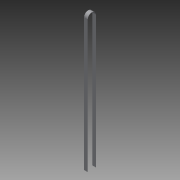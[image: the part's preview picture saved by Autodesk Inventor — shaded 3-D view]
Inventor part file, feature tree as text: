
AUTODESK INVENTOR PART (.ipt)
format: ipt  version: 2013 (Build 170138000, 138)  size: 89,088 bytes
history: native  units: in
note: dims shown in document units (in); Inventor stores cm internally (conversion verified against a paired STEP export)
features: extrude x1, sketch x1
ambient origin geometry x8: Origin, YZ Plane, XZ Plane, XY Plane, X Axis, Y Axis, Z Axis, Center Point
feature tree (2):
  extrude  "Extrusion2"  Depth=36.0in
  sketch  "Sketch1"  dims[d6=1.1in d7=36.0in d12=0.01in d13=1.0in d14=0.0in]
